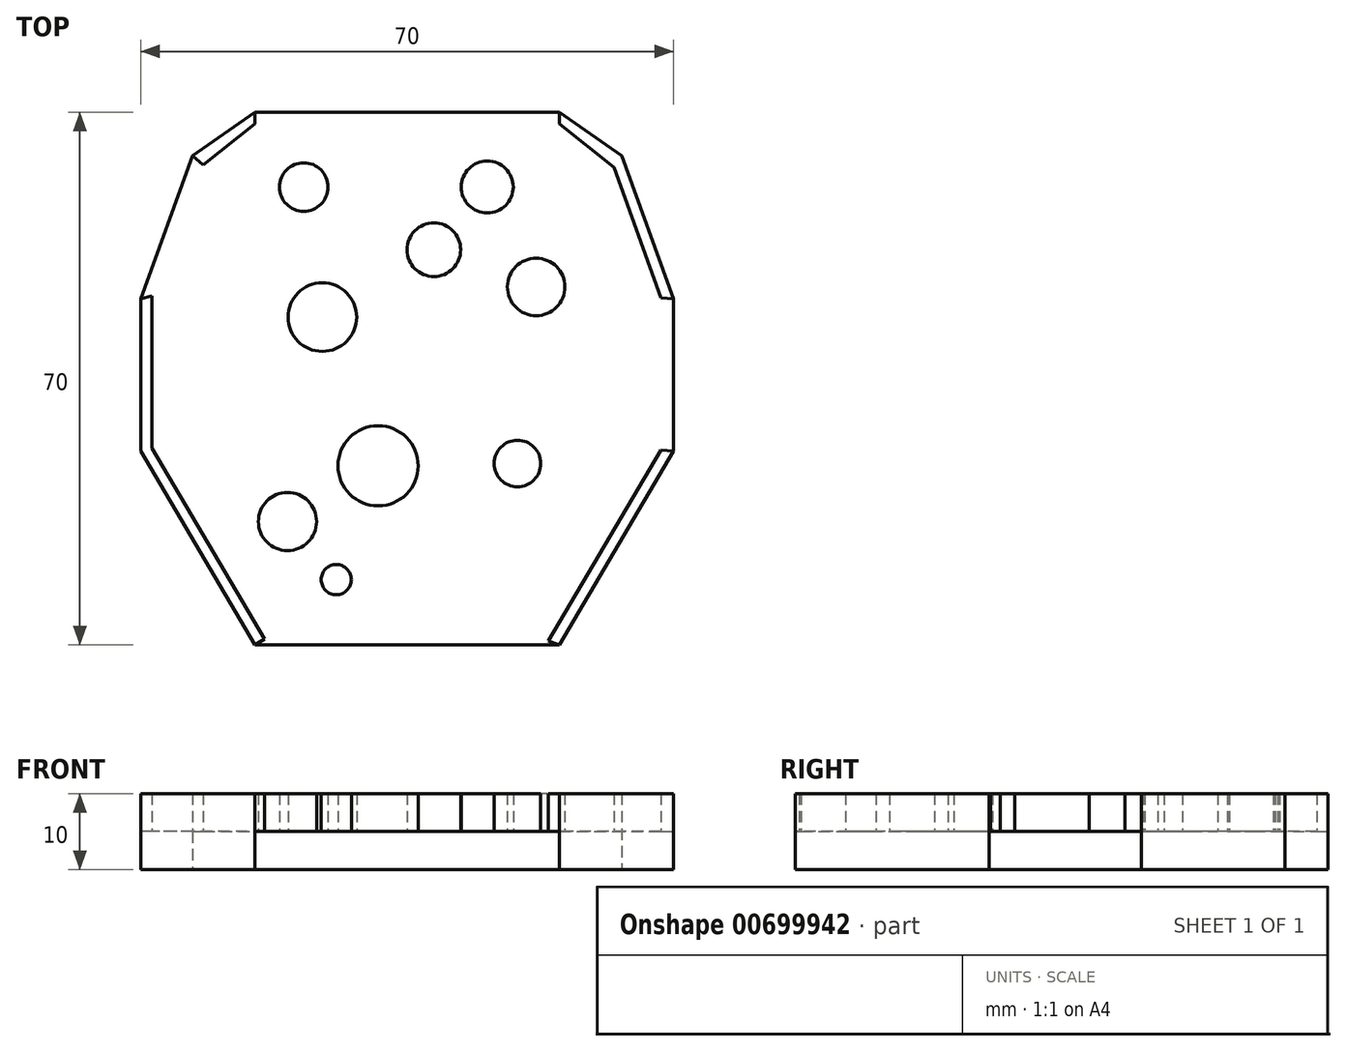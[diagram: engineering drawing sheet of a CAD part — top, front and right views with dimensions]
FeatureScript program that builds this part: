
annotation { "Feature Type Name" : "Feature", "Feature Type Description" : "" }
export const myFeature = defineFeature(function(context is Context, id is Id, definition is map)
    precondition{}
    {
        {
            var Q0;
            Q0=qCreatedBy(makeId("Top.planeOp"),FACE);
            var sketch = newSketch(context, id + "F0", { "sketchPlane" : qUnion([Q0])});
            skLineSegment(sketch, "E0.bottom", {"start": v(35, -35) * mm, "end": v(-35, -35) * mm});
            skLineSegment(sketch, "E0.top", {"start": v(35, 35) * mm, "end": v(-35, 35) * mm});
            skLineSegment(sketch, "E0.left", {"start": v(35, -35) * mm, "end": v(35, 35) * mm});
            skLineSegment(sketch, "E0.right", {"start": v(-35, -35) * mm, "end": v(-35, 35) * mm});
            skPoint(sketch, "E0.middle", {"position": v(0, 0) * mm});
            skLineSegment(sketch, "E1", {"start": v(0, 0) * mm, "end": v(-20, 35) * mm});
            skLineSegment(sketch, "E2", {"start": v(-20, 35) * mm, "end": v(20, 35) * mm});
            skLineSegment(sketch, "E3", {"start": v(20, 35) * mm, "end": v(0, 0) * mm});
            skLineSegment(sketch, "E4", {"start": v(-20, 35) * mm, "end": v(-28.2, 29.29) * mm});
            skLineSegment(sketch, "E5", {"start": v(-28.2, 29.29) * mm, "end": v(0, 0) * mm});
            skLineSegment(sketch, "E6", {"start": v(20, 35) * mm, "end": v(28.2, 29.29) * mm});
            skLineSegment(sketch, "E7", {"start": v(28.2, 29.29) * mm, "end": v(0, 0) * mm});
            skLineSegment(sketch, "E8", {"start": v(-28.2, 29.29) * mm, "end": v(-35, 10.47) * mm});
            skLineSegment(sketch, "E9", {"start": v(-35, 10.47) * mm, "end": v(0, 0) * mm});
            skLineSegment(sketch, "E10", {"start": v(28.2, 29.29) * mm, "end": v(35, 10.47) * mm});
            skLineSegment(sketch, "E11", {"start": v(35, 10.47) * mm, "end": v(0, 0) * mm});
            skLineSegment(sketch, "E12", {"start": v(-35, 10.47) * mm, "end": v(-35, -9.53) * mm});
            skLineSegment(sketch, "E13", {"start": v(35, 10.47) * mm, "end": v(35, -9.53) * mm});
            skLineSegment(sketch, "E14", {"start": v(-35, -9.53) * mm, "end": v(0, 0) * mm});
            skLineSegment(sketch, "E15", {"start": v(35, -9.53) * mm, "end": v(0, 0) * mm});
            skLineSegment(sketch, "E16", {"start": v(-35, -9.53) * mm, "end": v(-20, -35) * mm});
            skLineSegment(sketch, "E17", {"start": v(-20, -35) * mm, "end": v(20, -35) * mm});
            skLineSegment(sketch, "E18", {"start": v(20, -35) * mm, "end": v(35, -9.53) * mm});
            skLineSegment(sketch, "E19", {"start": v(-20, -35) * mm, "end": v(0, 0) * mm});
            skLineSegment(sketch, "E20", {"start": v(20, -35) * mm, "end": v(0, 0) * mm});
            skSolve(sketch);
        }
        {
            var Q0;
            Q0=makeQuery(id+"F0.imprint","IMPRINT",FACE,{"disambiguationData":[TD([[makeQuery(id+"F0.imprint","IMPRINT",EDGE,{"derivedFrom":sQuery(id+"F0.wireOp",EDGE,"E1")}),1.0]])]});
            var Q1;
            {var subQ2=sQuery(id+"F0.wireOp",EDGE,"E1");Q1=makeQuery(id+"F0.imprint","IMPRINT",FACE,{"disambiguationData":[TD([[makeQuery(id+"F0.imprint","IMPRINT",EDGE,{"derivedFrom":subQ2}),-1.0]])]});}
            var Q2;
            Q2=makeQuery(id+"F0.imprint","IMPRINT",FACE,{"disambiguationData":[TD([[makeQuery(id+"F0.imprint","IMPRINT",EDGE,{"derivedFrom":sQuery(id+"F0.wireOp",EDGE,"E3")}),1.0]])]});
            var Q3;
            Q3=makeQuery(id+"F0.imprint","IMPRINT",FACE,{"disambiguationData":[TD([[makeQuery(id+"F0.imprint","IMPRINT",EDGE,{"derivedFrom":sQuery(id+"F0.wireOp",EDGE,"E7")}),1.0]])]});
            var Q4;
            {var subQ0=sQuery(id+"F0.wireOp",EDGE,"E11");Q4=makeQuery(id+"F0.imprint","IMPRINT",FACE,{"disambiguationData":[TD([[makeQuery(id+"F0.imprint","IMPRINT",EDGE,{"derivedFrom":subQ0}),1.0]])]});}
            var Q5;
            Q5=makeQuery(id+"F0.imprint","IMPRINT",FACE,{"disambiguationData":[TD([[makeQuery(id+"F0.imprint","IMPRINT",EDGE,{"derivedFrom":sQuery(id+"F0.wireOp",EDGE,"E15")}),1.0]])]});
            var Q6;
            {var subQ2=sQuery(id+"F0.wireOp",EDGE,"E19");Q6=makeQuery(id+"F0.imprint","IMPRINT",FACE,{"disambiguationData":[TD([[makeQuery(id+"F0.imprint","IMPRINT",EDGE,{"derivedFrom":subQ2}),-1.0]])]});}
            var Q7;
            Q7=makeQuery(id+"F0.imprint","IMPRINT",FACE,{"disambiguationData":[TD([[makeQuery(id+"F0.imprint","IMPRINT",EDGE,{"derivedFrom":sQuery(id+"F0.wireOp",EDGE,"E14")}),-1.0]])]});
            var Q8;
            {var subQ0=sQuery(id+"F0.wireOp",EDGE,"E9");Q8=makeQuery(id+"F0.imprint","IMPRINT",FACE,{"disambiguationData":[TD([[makeQuery(id+"F0.imprint","IMPRINT",EDGE,{"derivedFrom":subQ0}),-1.0]])]});}
            var Q9;
            Q9=makeQuery(id+"F0.imprint","IMPRINT",FACE,{"disambiguationData":[TD([[makeQuery(id+"F0.imprint","IMPRINT",EDGE,{"derivedFrom":sQuery(id+"F0.wireOp",EDGE,"E5")}),-1.0]])]});
            extrude(context, id + "F1", {"entities" : qUnion([Q0, Q1, Q2, Q3, Q4, Q5, Q6, Q7, Q8, Q9]), "endBound" : BoundingType.SYMMETRIC, "depth" : 5 * mm, "offsetDistance" : 25 * mm, "hasSecondDirection" : true, "secondDirectionOppositeDirection" : true, "secondDirectionDepth" : 25 * mm});
        }
        {
            var Q0;
            Q0=makeQuery(id+"F1.opExtrude","CAP_FACE",FACE,{"disambiguationData":[OSD([sQuery(id+"F0.wireOp",EDGE,"E0.bottom"),sQuery(id+"F0.wireOp",EDGE,"E0.top"),sQuery(id+"F0.wireOp",EDGE,"E0.left"),sQuery(id+"F0.wireOp",EDGE,"E0.right"),sQuery(id+"F0.wireOp",EDGE,"E4"),sQuery(id+"F0.wireOp",EDGE,"E6"),sQuery(id+"F0.wireOp",EDGE,"E8"),sQuery(id+"F0.wireOp",EDGE,"E10"),sQuery(id+"F0.wireOp",EDGE,"E16"),sQuery(id+"F0.wireOp",EDGE,"E18")])],"isStart":false});
            var sketch = newSketch(context, id + "F2", { "sketchPlane" : qUnion([Q0])});
            skLineSegment(sketch, "E21", {"start": v(-20, -35) * mm, "end": v(-18.7, -34.24) * mm});
            skLineSegment(sketch, "E22", {"start": v(-18.7, -34.24) * mm, "end": v(-33.5, -9.12) * mm});
            skLineSegment(sketch, "E23", {"start": v(-35, -9.53) * mm, "end": v(-33.5, -9.12) * mm});
            skLineSegment(sketch, "E24", {"start": v(-33.5, -9.12) * mm, "end": v(-33.5, 10.88) * mm});
            skLineSegment(sketch, "E25", {"start": v(-33.5, 10.88) * mm, "end": v(-35, 10.47) * mm});
            skLineSegment(sketch, "E26", {"start": v(-35, 10.47) * mm, "end": v(-33.5, 10.88) * mm});
            skLineSegment(sketch, "E27", {"start": v(-28.2, 29.29) * mm, "end": v(-26.8, 28.07) * mm});
            skLineSegment(sketch, "E28", {"start": v(-26.8, 28.07) * mm, "end": v(-20, 33.5) * mm});
            skLineSegment(sketch, "E29", {"start": v(-20, 33.5) * mm, "end": v(-20, 35) * mm});
            skLineSegment(sketch, "E30", {"start": v(-20, 35) * mm, "end": v(-20, 33.5) * mm});
            skLineSegment(sketch, "E31", {"start": v(-20, 33.5) * mm, "end": v(20, 33.5) * mm});
            skLineSegment(sketch, "E32", {"start": v(20, 33.5) * mm, "end": v(20, 35) * mm});
            skLineSegment(sketch, "E33", {"start": v(20, 33.5) * mm, "end": v(27.15, 27.79) * mm});
            skLineSegment(sketch, "E34", {"start": v(27.15, 27.79) * mm, "end": v(28.2, 29.29) * mm});
            skLineSegment(sketch, "E35", {"start": v(27.15, 27.79) * mm, "end": v(33.35, 10.63) * mm});
            skLineSegment(sketch, "E36", {"start": v(33.35, 10.63) * mm, "end": v(35, 10.47) * mm});
            skLineSegment(sketch, "E37", {"start": v(35, 10.47) * mm, "end": v(33.35, 10.63) * mm});
            skLineSegment(sketch, "E38", {"start": v(33.35, 10.63) * mm, "end": v(33.35, -9.37) * mm});
            skLineSegment(sketch, "E39", {"start": v(33.35, -9.37) * mm, "end": v(35, -9.53) * mm});
            skLineSegment(sketch, "E40", {"start": v(-26.8, 28.07) * mm, "end": v(-33.5, 10.88) * mm});
            skLineSegment(sketch, "E41", {"start": v(33.35, -9.37) * mm, "end": v(18.56, -34.5) * mm});
            skLineSegment(sketch, "E42", {"start": v(18.56, -34.5) * mm, "end": v(20, -35) * mm});
            skCircle(sketch, "E43", {"center": v(-13.58, 25.18) * mm, "radius": 3.19 * mm});
            skCircle(sketch, "E44", {"center": v(16.94, 12.06) * mm, "radius": 3.78 * mm});
            skCircle(sketch, "E45", {"center": v(14.5, -11.14) * mm, "radius": 3.06 * mm});
            skCircle(sketch, "E46", {"center": v(-15.72, -18.77) * mm, "radius": 3.82 * mm});
            skCircle(sketch, "E47", {"center": v(-9.3, -26.4) * mm, "radius": 1.98 * mm});
            skCircle(sketch, "E48", {"center": v(-11.14, 8.09) * mm, "radius": 4.5 * mm});
            skCircle(sketch, "E49", {"center": v(10.53, 25.18) * mm, "radius": 3.41 * mm});
            skCircle(sketch, "E50", {"center": v(3.51, 16.94) * mm, "radius": 3.52 * mm});
            skCircle(sketch, "E51", {"center": v(-3.82, -11.45) * mm, "radius": 5.27 * mm});
            skSolve(sketch);
        }
        {
            var Q0;
            Q0 = qSketchRegion(id + "F2", true);
            var Q1;
            Q1=makeQuery(id+"F2.imprint","IMPRINT",FACE,{"disambiguationData":[TD([[makeQuery(id+"F2.imprint","IMPRINT",EDGE,{"derivedFrom":sQuery(id+"F2.wireOp",EDGE,"E27")}),1.0]])]});
            var Q2;
            Q2=makeQuery(id+"F2.imprint","IMPRINT",FACE,{"disambiguationData":[TD([[makeQuery(id+"F2.imprint","IMPRINT",EDGE,{"derivedFrom":sQuery(id+"F2.wireOp",EDGE,"E32")}),-1.0]])]});
            var Q3;
            Q3=makeQuery(id+"F2.imprint","IMPRINT",FACE,{"disambiguationData":[TD([[makeQuery(id+"F2.imprint","IMPRINT",EDGE,{"derivedFrom":sQuery(id+"F2.wireOp",EDGE,"E34")}),-1.0]])]});
            var Q4;
            Q4=makeQuery(id+"F2.imprint","IMPRINT",FACE,{"disambiguationData":[TD([[makeQuery(id+"F2.imprint","IMPRINT",EDGE,{"derivedFrom":sQuery(id+"F2.wireOp",EDGE,"E37")}),1.0]])]});
            var Q5;
            Q5=makeQuery(id+"F2.imprint","IMPRINT",FACE,{"disambiguationData":[TD([[makeQuery(id+"F2.imprint","IMPRINT",EDGE,{"derivedFrom":sQuery(id+"F2.wireOp",EDGE,"E39")}),-1.0]])]});
            var Q6;
            Q6=makeQuery(id+"F2.imprint","IMPRINT",FACE,{"disambiguationData":[TD([[makeQuery(id+"F2.imprint","IMPRINT",EDGE,{"derivedFrom":sQuery(id+"F2.wireOp",EDGE,"E21")}),1.0]])]});
            var Q7;
            Q7=makeQuery(id+"F2.imprint","IMPRINT",FACE,{"disambiguationData":[TD([[makeQuery(id+"F2.imprint","IMPRINT",EDGE,{"derivedFrom":sQuery(id+"F2.wireOp",EDGE,"E23")}),1.0]])]});
            var Q8;
            Q8=makeQuery(id+"F2.imprint","IMPRINT",FACE,{"disambiguationData":[TD([[makeQuery(id+"F2.imprint","IMPRINT",EDGE,{"derivedFrom":sQuery(id+"F2.wireOp",EDGE,"E26")}),1.0]])]});
            extrude(context, id + "F3", {"entities" : qUnion([Q0, Q1, Q2, Q3, Q4, Q5, Q6, Q7, Q8]), "operationType" : NewBodyOperationType.ADD, "depth" : 5 * mm, "offsetDistance" : 25 * mm});
        }
    });
